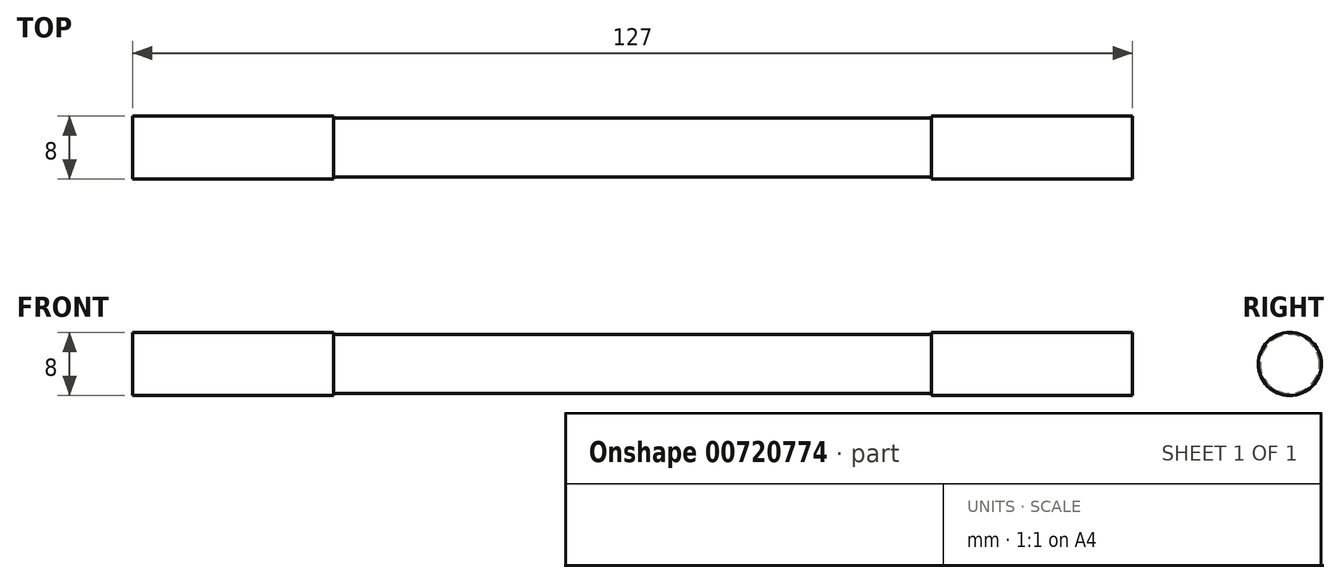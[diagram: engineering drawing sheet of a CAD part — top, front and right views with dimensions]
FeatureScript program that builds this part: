
annotation { "Feature Type Name" : "Feature", "Feature Type Description" : "" }
export const myFeature = defineFeature(function(context is Context, id is Id, definition is map)
    precondition{}
    {
        {
            var Q0;
            Q0=qCreatedBy(makeId("Top.planeOp"),FACE);
            var sketch = newSketch(context, id + "F0", { "sketchPlane" : qUnion([Q0])});
            skLineSegment(sketch, "E0.bottom", {"start": v(63.5, -4) * mm, "end": v(-63.5, -4) * mm});
            skLineSegment(sketch, "E0.top", {"start": v(63.5, 4) * mm, "end": v(-63.5, 4) * mm});
            skLineSegment(sketch, "E0.left", {"start": v(63.5, -4) * mm, "end": v(63.5, 4) * mm});
            skLineSegment(sketch, "E0.right", {"start": v(-63.5, -4) * mm, "end": v(-63.5, 4) * mm});
            skPoint(sketch, "E0.middle", {"position": v(0, 0) * mm});
            skLineSegment(sketch, "E1", {"start": v(0, 0) * mm, "end": v(38, 0) * mm, "construction": true});
            skLineSegment(sketch, "E2", {"start": v(0, 0) * mm, "end": v(-38, 0) * mm, "construction": true});
            skLineSegment(sketch, "E3", {"start": v(-38, 4) * mm, "end": v(-38, -4) * mm});
            skLineSegment(sketch, "E4", {"start": v(38, 4) * mm, "end": v(38, -4) * mm});
            skLineSegment(sketch, "E5", {"start": v(-38, 3.75) * mm, "end": v(38, 3.75) * mm});
            skLineSegment(sketch, "E6", {"start": v(-38, -3.75) * mm, "end": v(38, -3.75) * mm});
            skLineSegment(sketch, "E7", {"start": v(-38, -3.75) * mm, "end": v(-38, -4) * mm, "construction": true});
            skLineSegment(sketch, "E8", {"start": v(-38, 4) * mm, "end": v(-38, 3.75) * mm, "construction": true});
            skLineSegment(sketch, "E9", {"start": v(-63.5, 0) * mm, "end": v(63.5, 0) * mm});
            skSolve(sketch);
        }
        {
            var Q0;
            {var subQ4=sQuery(id+"F0.wireOp",EDGE,"E0.right");var subQ5=sQuery(id+"F0.wireOp",EDGE,"E0.top");var subQ6=makeQuery(id+"F0.imprint","INTERSECT",VERTEX,{"derivedFrom":[subQ5,subQ4]});Q0=makeQuery(id+"F0.imprint","IMPRINT",FACE,{"disambiguationData":[TD([[makeQuery(id+"F0.imprint","IMPRINT",EDGE,{"disambiguationData":[TD([[subQ6,1.0]])],"derivedFrom":subQ5}),1.0]])]});}
            var Q1;
            {var subQ0=sQuery(id+"F0.wireOp",EDGE,"E5");Q1=makeQuery(id+"F0.imprint","IMPRINT",FACE,{"disambiguationData":[TD([[makeQuery(id+"F0.imprint","IMPRINT",EDGE,{"derivedFrom":subQ0}),-1.0]])]});}
            var Q2;
            {var subQ4=sQuery(id+"F0.wireOp",EDGE,"E0.top");var subQ6=sQuery(id+"F0.wireOp",EDGE,"E0.left");var subQ7=makeQuery(id+"F0.imprint","INTERSECT",VERTEX,{"derivedFrom":[subQ4,subQ6]});Q2=makeQuery(id+"F0.imprint","IMPRINT",FACE,{"disambiguationData":[TD([[makeQuery(id+"F0.imprint","IMPRINT",EDGE,{"disambiguationData":[TD([[subQ7,-1.0]])],"derivedFrom":subQ4}),1.0]])]});}
            var Q3;
            Q3=sQuery(id+"F0.wireOp",EDGE,"E9");
            revolve(context, id + "F1", {"surfaceOperationType" : NewSurfaceOperationType.NEW, "entities" : qUnion([Q0, Q1, Q2]), "axis" : qUnion([Q3]), "revolveType" : RevolveType.FULL});
        }
    });
